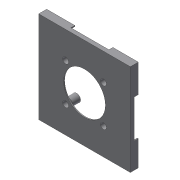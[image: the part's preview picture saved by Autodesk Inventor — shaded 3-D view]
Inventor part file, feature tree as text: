
AUTODESK INVENTOR PART (.ipt)
format: ipt  version: 2017 (Build 210142000, 142)  size: 328,192 bytes
history: native  units: mm
features: sketch x9, extrude x7, projected_geometry x5, pattern_circular x2, hole x1, fillet x1
ambient origin geometry x8: Origin, YZ Plane, XZ Plane, XY Plane, X Axis, Y Axis, Z Axis, Center Point
bodies: Solid1 (feature_tree)
feature tree (25):
  extrude  "Extrusion1"  Depth=90.0mm
  sketch  "Sketch2"  dims[d2=92.0mm d3=92.0mm]
  extrude  "Extrusion2"  Depth=92.0mm
  extrude  "Extrusion3"  Depth=90.0mm
  hole  "Hole1"  [1 undecoded]
  pattern_circular  "Circular Pattern2"  [2 undecoded]
  extrude  "Extrusion4"  Depth=2.0mm
  extrude  "Extrusion5"  Depth=2.0mm
  extrude  "Extrusion6"  Depth=10.0mm TaperAngle=0.0deg
  extrude  "Extrusion7"  Depth=2.0mm
  fillet  "Fillet1"  Radius=27.0mm
  pattern_circular  "Circular Pattern3"  Count=4 Angle=360.0deg
  sketch  "Sketch1"  dims[d0=90.0mm d1=90.0mm]
  projected_geometry  "Projected Loop1"
  sketch  "Sketch3"  dims[d4=1.0mm d5=0.0mm d6=90.0mm]
  sketch  "Sketch4"  dims[d7=90.0mm d8=1.0mm]
  projected_geometry  "Projected Loop2"
  projected_geometry  "Projected Loop3"
  sketch  "Sketch5"  dims[d9=1.0mm]
  sketch  "Sketch6"  dims[d10=10.0mm]
  sketch  "Sketch7"  dims[d11=10.0mm]
  sketch  "Sketch8"  dims[d12=14.5mm]
  projected_geometry  "Projected Loop4"
  sketch  "Sketch9"  dims[d13=17.25mm d14=7.0mm d15=0.0mm d16=22.5mm d17=8.625mm d18=10.0mm d19=0.0mm d23=27.0mm d24=27.0mm d25=4.0mm d26=6.0mm d27=4.0mm d28=2.0mm d29=90.0deg d30=8.0mm d31=20.594885mm d32=40.0mm d33=360.0deg d35=42.0mm d36=10.0mm d37=0.0mm d38=90.0mm d39=90.0mm d40=3.0mm d41=0.0mm d42=8.0mm d43=10.0mm d44=0.0mm d45=6.0mm d46=10.0mm d47=0.0mm d48=2.0mm d49=40.0mm d50=360.0deg]
  projected_geometry  "Projected Loop5"
note: 3 required parameter values undecoded (feature->parameter linkage not recoverable at this tier; creation-order binding heuristic only, values carry confidence <= 0.55)
